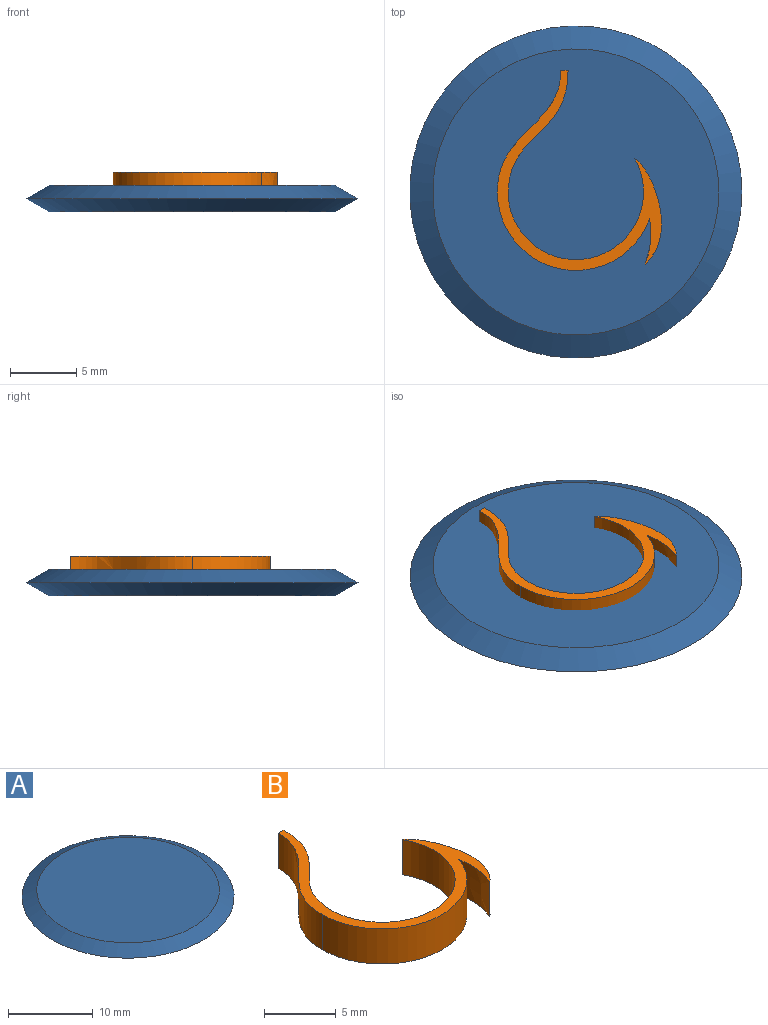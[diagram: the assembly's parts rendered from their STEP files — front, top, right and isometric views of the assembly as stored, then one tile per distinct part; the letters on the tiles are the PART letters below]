
ASSEMBLY  parts=2 mates=1
PART A: 4 faces, bbox 25x25x2 mm
  f0: plane 21.54x21.54mm, normal (0,0,1), area 364.3mm2, adj f1
  f1: cone r=12.5mm half-angle=60deg, axis (0,0,-1), area 146.2mm2, adj f0,f2
  f2: cone r=12.5mm half-angle=60deg, axis (0,0,1), area 146.2mm2, adj f1,f3
  f3: plane 21.54x21.54mm, normal (0,0,-1), area 364.3mm2, adj f2
PART B: 9 faces, bbox 12.9x15.1x3 mm
  f0: cylinder r=5.1mm len=10.19mm, axis (0,0,-1), area 55.2mm2, adj f1,f6,f7,f8
  f1: extruded ~7.92x3mm, area 26.5mm2, adj f0,f2,f7,f8
  f2: extruded ~3.42x3mm, area 10.5mm2, adj f1,f3,f7,f8
  f3: cylinder r=5.91mm len=11.46mm, axis (0,0,-1), area 49.5mm2, adj f2,f4,f7,f8
  f4: extruded ~9.16x4.78mm, area 32mm2, adj f3,f5,f7,f8
  f5: plane 3x0.54mm, normal (0,1,0), area 1.6mm2, adj f4,f6,f7,f8
  f6: extruded ~9.36x4.51mm, area 32.3mm2, adj f0,f5,f7,f8
  f7: plane 15.07x12.91mm, normal (0,0,1), area 26mm2, adj f0,f1,f2,f3,f4,f5,f6
  f8: plane 15.07x12.91mm, normal (0,0,-1), area 26mm2, adj f0,f1,f2,f3,f4,f5,f6
PLACE A t=(-90.11,-1.35,-0.33)mm
PLACE B t=(-90.11,-1.35,-0.33)mm
MATE fastened A.f1 <-> B.f3  axis (0,0,1) through (-0.11,-1.35,0.67)mm
